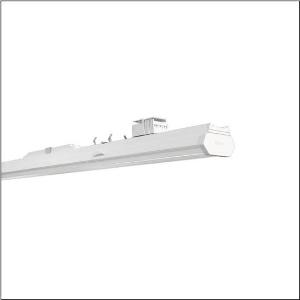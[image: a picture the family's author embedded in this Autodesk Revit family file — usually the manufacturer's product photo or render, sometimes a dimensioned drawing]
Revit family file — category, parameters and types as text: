
# Revit family: licross_r__21_protected_mo_52td12dn4a5g3c_a968
name_source: partatom
category: Lighting Fixtures
units: mm (PartAtom-declared; Revit-internal decimal feet)

## family parameters
Cut with Voids When Loaded = No
Host = Face
Light Source = No
Part Type = Normal
Room Calculation Point = No
Round Connector Dimension = Use Diameter
Shared = No

## types (1)
- --- (1 x LED, 940 lm, 6.8 W, 4000K)
    Apparent Load = 7 VA
    CIE Flux Codes = 73 92 98 99 100
    Color Rendering = 80
    Color Temperature = 4000K
    Default Elevation = 1800 mm
    Description = Licross® 21 Protected MO, luminaire insert, of sheet steel, galvanised, coil coated, white, length: 1.500mm, width: 90mm, height: 103mm, LED rated luminous flux: 10.700lm, light colour: 840, control gear: DALI 2, with plug, 6-pole, with phase selection, for trunking rail, 14-core, mains connection: 220..240V, AC, 50/60Hz, rated input power: 66W, for trunking rail, 14-core, halogen-free wiring, for emergency light function, converter,control gear: single battery element, battery: LiFeP04, 9Ah, primary light control with lens, of plastic, primary optical cover: cover, of PMMA, light emission: direct distribution, primary light characteristic: symmetric, protection rating (complete): IP54, insulation class (complete): insulation class I (protective earthing), certification: CE, UKCA, protection symbol: D if used in an environment with non-conductive dust loads with corresponding accessories, impact resistance: IK06, permissible ambient temperature for indoor applications: +5..+35°C, standard: EN 60598-2-22, LABS conformity tested according to VDMA 24364:2018-05, reducing of maximum allowable ambient temperature of 5°C with ceiling mounting, corresponds to IFS (International Featured Standards) requirements for safety and quality in the food industry, packaging unit: 1 piece
    Height = 92 mm
    Lamp = 1 x LED
    Lamp Light Flux = 940 lm
    Lamp Power = 6.8 W
    Lamp count = 1
    Length = 1500 mm
    Luminous efficacy = 138 lm/W
    Manufacturer = Siteco
    ModVariant = No
    Model = 52TD12DN4A5G3C
    Mounting Place = Ceiling
    Mounting Type = Pendant
    Number of Poles = 1
    OnlyDefault = Yes
    Power Factor = 1
    Product Name = Licross® 21 Protected MO
    Product group = luminaire insert
    ProductGroupID = 901
    Protection Class = Protection class I
    Protection Degree = IP 54
    RLX_Detail_Level = 1
    RLX_Emergency_Light_Flux = 0 lm
    RLX_Emergency_Type = 0
    RLX_Emergency_Type_DB = No
    RlxData = <blob elided: 24733 chars, md5=e74eb8b3>
    Socket = socket
    Standby Power = 0 W
    System Light Flux = 940 lm
    System Power = 7 W
    Type Comments = : emergency light operation: 3 h
    Type Image = l_1256148.jpg
    URL = http://relux.com
    VarID = @adj_059173
    Voltage = 0 V
    Weight = 0.00 kg
    Width = 88 mm

## geometry (parser evidence)
native form markers: Blend x4, Sweep x9
no freeform markers — native parametric forms only
